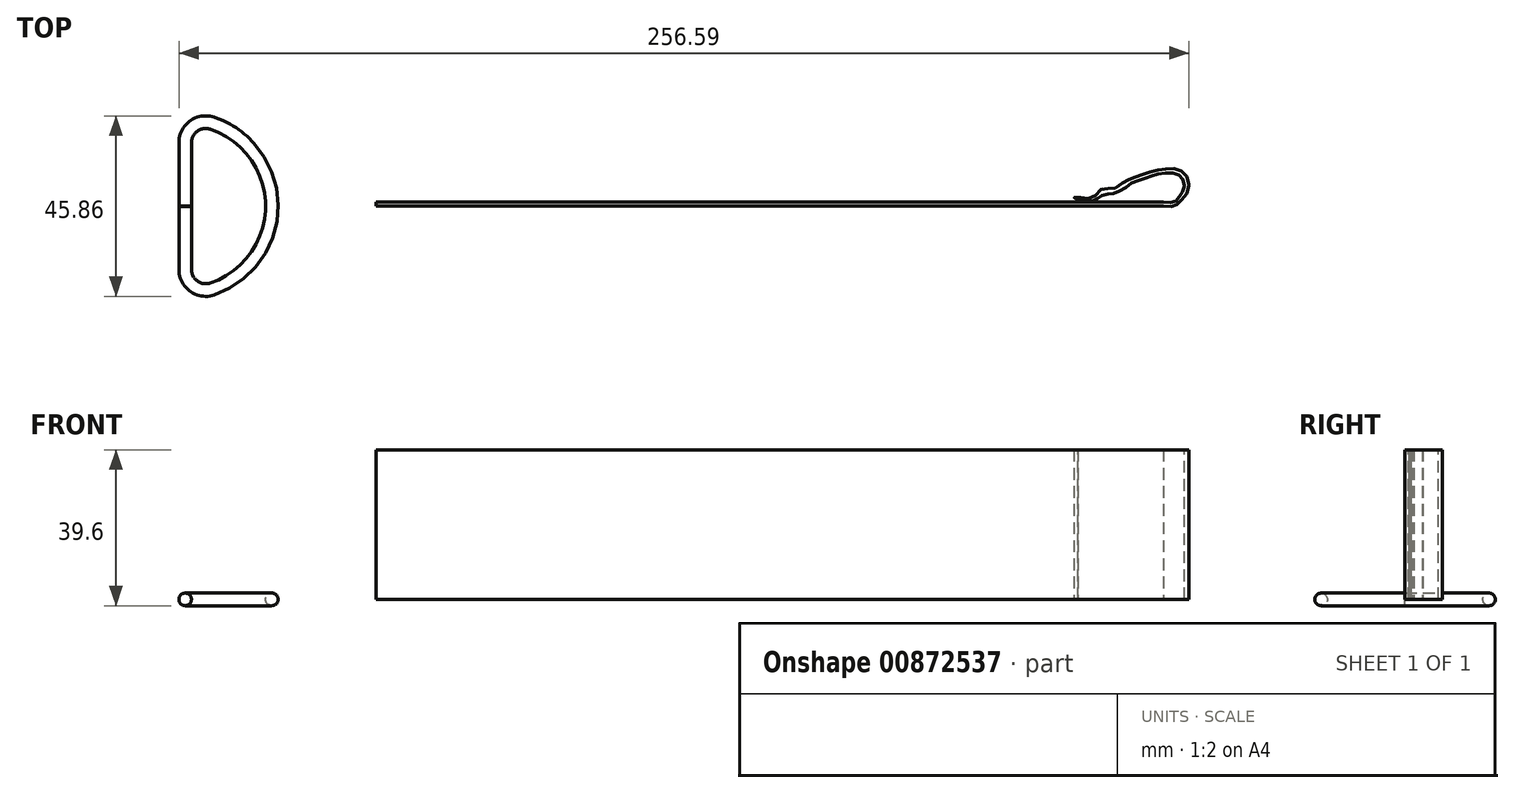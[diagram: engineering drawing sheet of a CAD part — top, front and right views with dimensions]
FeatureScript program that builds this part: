
annotation { "Feature Type Name" : "Feature", "Feature Type Description" : "" }
export const myFeature = defineFeature(function(context is Context, id is Id, definition is map)
    precondition{}
    {
        {
            var Q0;
            Q0=qCreatedBy(makeId("Top.planeOp"),FACE);
            var sketch = newSketch(context, id + "F0", { "sketchPlane" : qUnion([Q0])});
            skLineSegment(sketch, "E0", {"start": v(-48.27, 0) * mm, "end": v(-48.27, 16.12) * mm});
            skArc(sketch, "E1", {"start": v(-41.68, -20.86) * mm, "mid": v(-26.68, 0) * mm, "end": v(-41.68, 20.86) * mm});
            skLineSegment(sketch, "E2", {"start": v(-48.27, -16.12) * mm, "end": v(-48.27, -0.1) * mm});
            skPoint(sketch, "E3.visualSharp", {"position": v(-48.27, -22) * mm});
            skArc(sketch, "E3.filletArc", {"start": v(-48.27, -16.12) * mm, "mid": v(-46.2, -20.18) * mm, "end": v(-41.68, -20.86) * mm});
            skPoint(sketch, "E4.visualSharp", {"position": v(-48.27, 22) * mm});
            skArc(sketch, "E4.filletArc", {"start": v(-41.68, 20.86) * mm, "mid": v(-46.2, 20.18) * mm, "end": v(-48.27, 16.12) * mm});
            skSolve(sketch);
        }
        {
            var Q0;
            Q0=qCreatedBy(makeId("Front.planeOp"),FACE);
            var sketch = newSketch(context, id + "F1", { "sketchPlane" : qUnion([Q0])});
            skCircle(sketch, "E5", {"center": v(-48.49, 0) * mm, "radius": 1.6 * mm});
            skSolve(sketch);
        }
        {
            var Q0;
            Q0=makeQuery(id+"F1.imprint","IMPRINT",FACE,{"disambiguationData":[TD([[makeQuery(id+"F1.imprint","IMPRINT",EDGE,{"derivedFrom":sQuery(id+"F1.wireOp",EDGE,"E5")}),1.0]])]});
            var Q1;
            Q1=sQuery(id+"F0.wireOp",EDGE,"E0");
            var Q2;
            Q2=sQuery(id+"F0.wireOp",EDGE,"E4.filletArc");
            var Q3;
            Q3=sQuery(id+"F0.wireOp",EDGE,"E1");
            var Q4;
            Q4=sQuery(id+"F0.wireOp",EDGE,"E3.filletArc");
            var Q5;
            Q5=sQuery(id+"F0.wireOp",EDGE,"E2");
            sweep(context, id + "F2", {"profiles" : qUnion([Q0]), "path" : qUnion([Q1, Q2, Q3, Q4, Q5])});
        }
        {
            var Q0;
            Q0=qCreatedBy(makeId("Top.planeOp"),FACE);
            var sketch = newSketch(context, id + "F3", { "sketchPlane" : qUnion([Q0])});
            skLineSegment(sketch, "E6.bottom", {"start": v(0, 0) * mm, "end": v(200, 0) * mm});
            skLineSegment(sketch, "E6.top", {"start": v(0, 1) * mm, "end": v(200, 1) * mm});
            skLineSegment(sketch, "E6.left", {"start": v(0, 0) * mm, "end": v(0, 1) * mm});
            skLineSegment(sketch, "E6.right", {"start": v(200, 0) * mm, "end": v(200, 1) * mm});
            skFitSpline(sketch, "E7", {"points": [v(200, 1) * mm, v(202.79, 1) * mm, v(204.02, 2.36) * mm, v(205.06, 3.9) * mm, v(205.18, 6.4) * mm, v(203.76, 8.06) * mm, v(201.15, 8.42) * mm, v(197.7, 7.94) * mm, v(195.69, 7.11) * mm, v(192.36, 6.04) * mm, v(189.94, 4.38) * mm, v(187.24, 3.2) * mm, v(185.58, 2.95) * mm, v(183.57, 2.16) * mm, v(182.3, 1.33) * mm, v(178.3, 1.55) * mm, v(178.3, 1.5) * mm], "startDerivative": vector(41.45, -0.98) * mm, "endDerivative": vector(-0.47, -15.09) * mm});
            skFitSpline(sketch, "E8", {"points": [v(200, 0) * mm, v(202.79, 0) * mm, v(204.02, 1) * mm, v(206.12, 3.43) * mm, v(206.12, 7.11) * mm, v(204.02, 9.19) * mm, v(200.96, 9.48) * mm, v(197.7, 8.94) * mm, v(194.6, 7.94) * mm, v(192.36, 7.11) * mm, v(189.94, 6.04) * mm, v(187.05, 4.38) * mm, v(184.37, 4.38) * mm, v(182.12, 2.16) * mm, v(179.28, 2.16) * mm, v(177.4, 2.16) * mm, v(178.3, 1.5) * mm], "startDerivative": vector(46.3, 0) * mm, "endDerivative": vector(67.48, -48.93) * mm});
            skSolve(sketch);
        }
        {
            var Q0;
            Q0=makeQuery(id+"F3.imprint","IMPRINT",FACE,{"disambiguationData":[TD([[makeQuery(id+"F3.imprint","IMPRINT",EDGE,{"derivedFrom":sQuery(id+"F3.wireOp",EDGE,"E6.bottom")}),1.0]])]});
            var Q1;
            Q1=makeQuery(id+"F3.imprint","IMPRINT",FACE,{"disambiguationData":[TD([[makeQuery(id+"F3.imprint","IMPRINT",EDGE,{"derivedFrom":sQuery(id+"F3.wireOp",EDGE,"E6.right")}),-1.0]])]});
            extrude(context, id + "F4", {"entities" : qUnion([Q0, Q1]), "depth" : 38 * mm, "offsetDistance" : 25 * mm});
        }
    });
